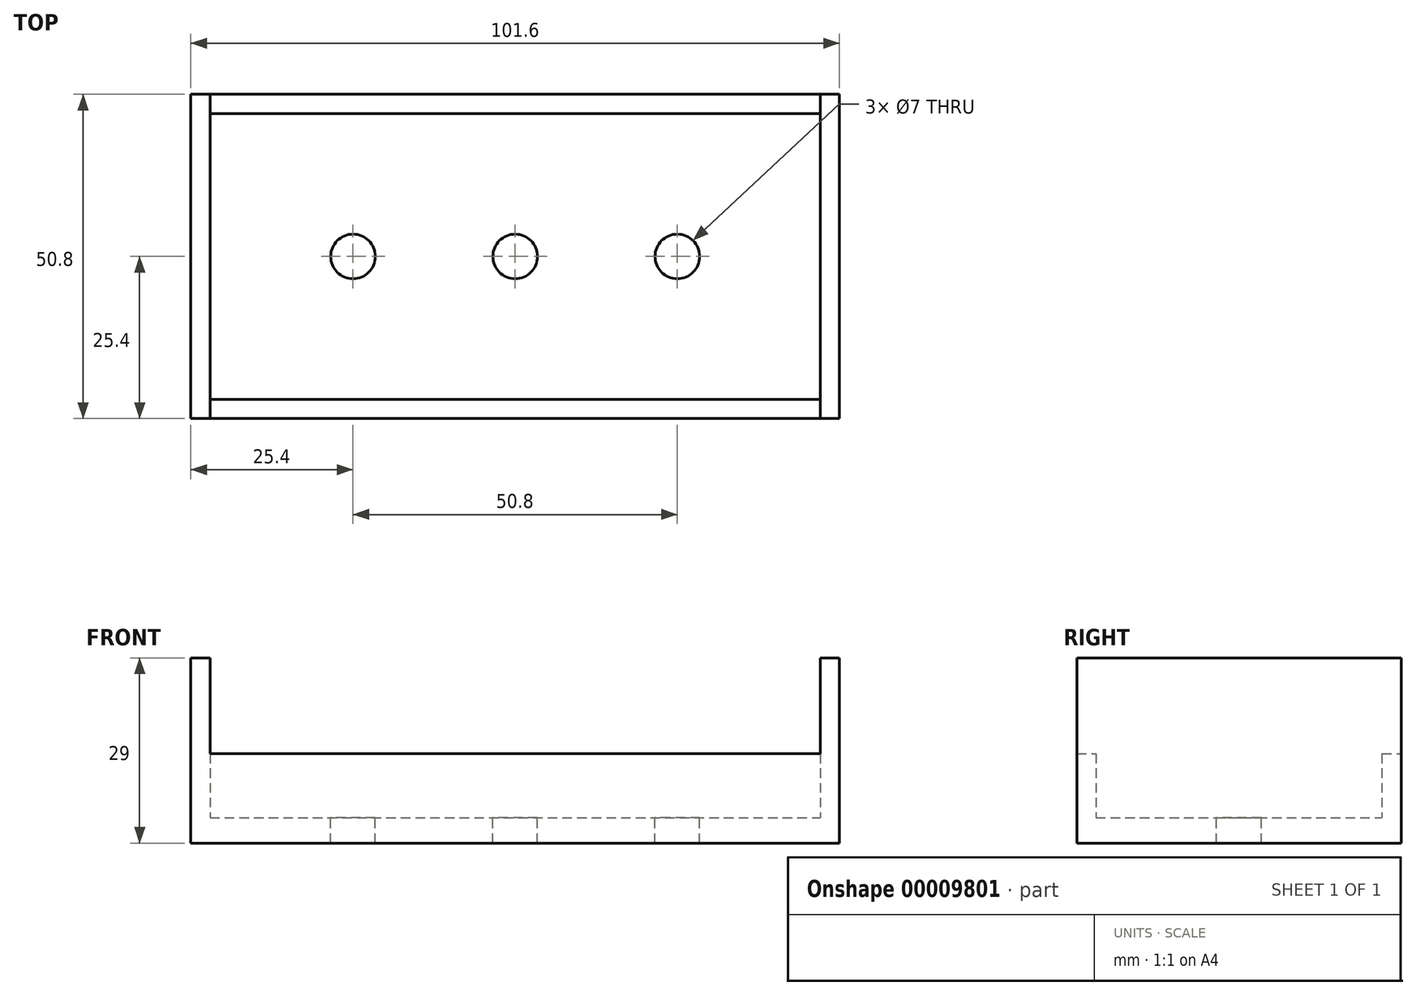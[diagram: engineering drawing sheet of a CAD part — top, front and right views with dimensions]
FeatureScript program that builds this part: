
annotation { "Feature Type Name" : "Feature", "Feature Type Description" : "" }
export const myFeature = defineFeature(function(context is Context, id is Id, definition is map)
    precondition{}
    {
        {
            var Q0;
            Q0=qCreatedBy(makeId("Top.planeOp"),FACE);
            var sketch = newSketch(context, id + "F0", { "sketchPlane" : qUnion([Q0])});
            skLineSegment(sketch, "E0.bottom", {"start": v(0, 0) * mm, "end": v(101.6, 0) * mm});
            skLineSegment(sketch, "E0.top", {"start": v(0, 50.8) * mm, "end": v(101.6, 50.8) * mm});
            skLineSegment(sketch, "E0.left", {"start": v(0, 0) * mm, "end": v(0, 50.8) * mm});
            skLineSegment(sketch, "E0.right", {"start": v(101.6, 0) * mm, "end": v(101.6, 50.8) * mm});
            skSolve(sketch);
        }
        {
            var Q0;
            Q0=makeQuery(id+"F0.imprint","IMPRINT",FACE,{"disambiguationData":[TD([[makeQuery(id+"F0.imprint","IMPRINT",EDGE,{"derivedFrom":sQuery(id+"F0.wireOp",EDGE,"E0.bottom")}),1.0]])]});
            extrude(context, id + "F1", {"entities" : qUnion([Q0]), "depth" : 4 * mm});
        }
        {
            var Q0;
            Q0=makeQuery(id+"F1.opExtrude","CAP_FACE",FACE,{"disambiguationData":[OSD([sQuery(id+"F0.wireOp",EDGE,"E0.bottom"),sQuery(id+"F0.wireOp",EDGE,"E0.top"),sQuery(id+"F0.wireOp",EDGE,"E0.left"),sQuery(id+"F0.wireOp",EDGE,"E0.right")])],"isStart":false});
            var sketch = newSketch(context, id + "F2", { "sketchPlane" : qUnion([Q0])});
            skCircle(sketch, "E1", {"center": v(25.4, 25.4) * mm, "radius": 3.5 * mm});
            skCircle(sketch, "E2", {"center": v(50.8, 25.4) * mm, "radius": 3.5 * mm});
            skCircle(sketch, "E3", {"center": v(76.2, 25.4) * mm, "radius": 3.5 * mm});
            skSolve(sketch);
        }
        {
            var Q0;
            Q0=makeQuery(id+"F2.imprint","IMPRINT",FACE,{"disambiguationData":[TD([[makeQuery(id+"F2.imprint","IMPRINT",EDGE,{"derivedFrom":sQuery(id+"F2.wireOp",EDGE,"E1")}),1.0]])]});
            var Q1;
            Q1=makeQuery(id+"F2.imprint","IMPRINT",FACE,{"disambiguationData":[TD([[makeQuery(id+"F2.imprint","IMPRINT",EDGE,{"derivedFrom":sQuery(id+"F2.wireOp",EDGE,"E2")}),1.0]])]});
            var Q2;
            Q2=makeQuery(id+"F2.imprint","IMPRINT",FACE,{"disambiguationData":[TD([[makeQuery(id+"F2.imprint","IMPRINT",EDGE,{"derivedFrom":sQuery(id+"F2.wireOp",EDGE,"E3")}),1.0]])]});
            extrude(context, id + "F3", {"entities" : qUnion([Q0, Q1, Q2]), "operationType" : NewBodyOperationType.REMOVE, "oppositeDirection" : true, "depth" : 25 * mm});
        }
        {
            var Q0;
            Q0=makeQuery(id+"F1.opExtrude","CAP_FACE",FACE,{"disambiguationData":[OSD([sQuery(id+"F0.wireOp",EDGE,"E0.bottom"),sQuery(id+"F0.wireOp",EDGE,"E0.top"),sQuery(id+"F0.wireOp",EDGE,"E0.left"),sQuery(id+"F0.wireOp",EDGE,"E0.right")])],"isStart":false});
            var sketch = newSketch(context, id + "F4", { "sketchPlane" : qUnion([Q0])});
            skLineSegment(sketch, "E4.bottom", {"start": v(0, 0) * mm, "end": v(3, 0) * mm});
            skLineSegment(sketch, "E4.top", {"start": v(0, 50.8) * mm, "end": v(3, 50.8) * mm});
            skLineSegment(sketch, "E4.left", {"start": v(0, 0) * mm, "end": v(0, 50.8) * mm});
            skLineSegment(sketch, "E4.right", {"start": v(3, 0) * mm, "end": v(3, 50.8) * mm});
            skLineSegment(sketch, "E5.bottom", {"start": v(101.6, 0) * mm, "end": v(98.6, 0) * mm});
            skLineSegment(sketch, "E5.top", {"start": v(101.6, 50.8) * mm, "end": v(98.6, 50.8) * mm});
            skLineSegment(sketch, "E5.left", {"start": v(101.6, 0) * mm, "end": v(101.6, 50.8) * mm});
            skLineSegment(sketch, "E5.right", {"start": v(98.6, 0) * mm, "end": v(98.6, 50.8) * mm});
            skSolve(sketch);
        }
        {
            var Q0;
            Q0=makeQuery(id+"F4.imprint","IMPRINT",FACE,{"disambiguationData":[TD([[makeQuery(id+"F4.imprint","IMPRINT",EDGE,{"derivedFrom":sQuery(id+"F4.wireOp",EDGE,"E5.bottom")}),1.0]])]});
            var Q1;
            Q1=makeQuery(id+"F4.imprint","IMPRINT",FACE,{"disambiguationData":[TD([[makeQuery(id+"F4.imprint","IMPRINT",EDGE,{"derivedFrom":sQuery(id+"F4.wireOp",EDGE,"E4.bottom")}),1.0]])]});
            extrude(context, id + "F5", {"entities" : qUnion([Q0, Q1]), "operationType" : NewBodyOperationType.ADD, "depth" : 25 * mm});
        }
        {
            var Q0;
            Q0=makeQuery(id+"F1.opExtrude","CAP_FACE",FACE,{"disambiguationData":[OSD([sQuery(id+"F0.wireOp",EDGE,"E0.bottom"),sQuery(id+"F0.wireOp",EDGE,"E0.top"),sQuery(id+"F0.wireOp",EDGE,"E0.left"),sQuery(id+"F0.wireOp",EDGE,"E0.right")])],"isStart":false});
            var sketch = newSketch(context, id + "F6", { "sketchPlane" : qUnion([Q0])});
            skLineSegment(sketch, "E6.bottom", {"start": v(3, 50.8) * mm, "end": v(98.6, 50.8) * mm});
            skLineSegment(sketch, "E6.top", {"start": v(3, 47.8) * mm, "end": v(98.6, 47.8) * mm});
            skLineSegment(sketch, "E6.left", {"start": v(3, 50.8) * mm, "end": v(3, 47.8) * mm});
            skLineSegment(sketch, "E6.right", {"start": v(98.6, 50.8) * mm, "end": v(98.6, 47.8) * mm});
            skLineSegment(sketch, "E7.bottom", {"start": v(3, 0) * mm, "end": v(98.6, 0) * mm});
            skLineSegment(sketch, "E7.top", {"start": v(3, 3) * mm, "end": v(98.6, 3) * mm});
            skLineSegment(sketch, "E7.left", {"start": v(3, 0) * mm, "end": v(3, 3) * mm});
            skLineSegment(sketch, "E7.right", {"start": v(98.6, 0) * mm, "end": v(98.6, 3) * mm});
            skSolve(sketch);
        }
        {
            var Q0;
            Q0=makeQuery(id+"F6.imprint","IMPRINT",FACE,{"disambiguationData":[TD([[makeQuery(id+"F6.imprint","IMPRINT",EDGE,{"derivedFrom":sQuery(id+"F6.wireOp",EDGE,"E6.bottom")}),-1.0]])]});
            var Q1;
            Q1=makeQuery(id+"F6.imprint","IMPRINT",FACE,{"disambiguationData":[TD([[makeQuery(id+"F6.imprint","IMPRINT",EDGE,{"derivedFrom":sQuery(id+"F6.wireOp",EDGE,"E7.bottom")}),1.0]])]});
            extrude(context, id + "F7", {"entities" : qUnion([Q0, Q1]), "operationType" : NewBodyOperationType.ADD, "depth" : 10 * mm});
        }
    });
